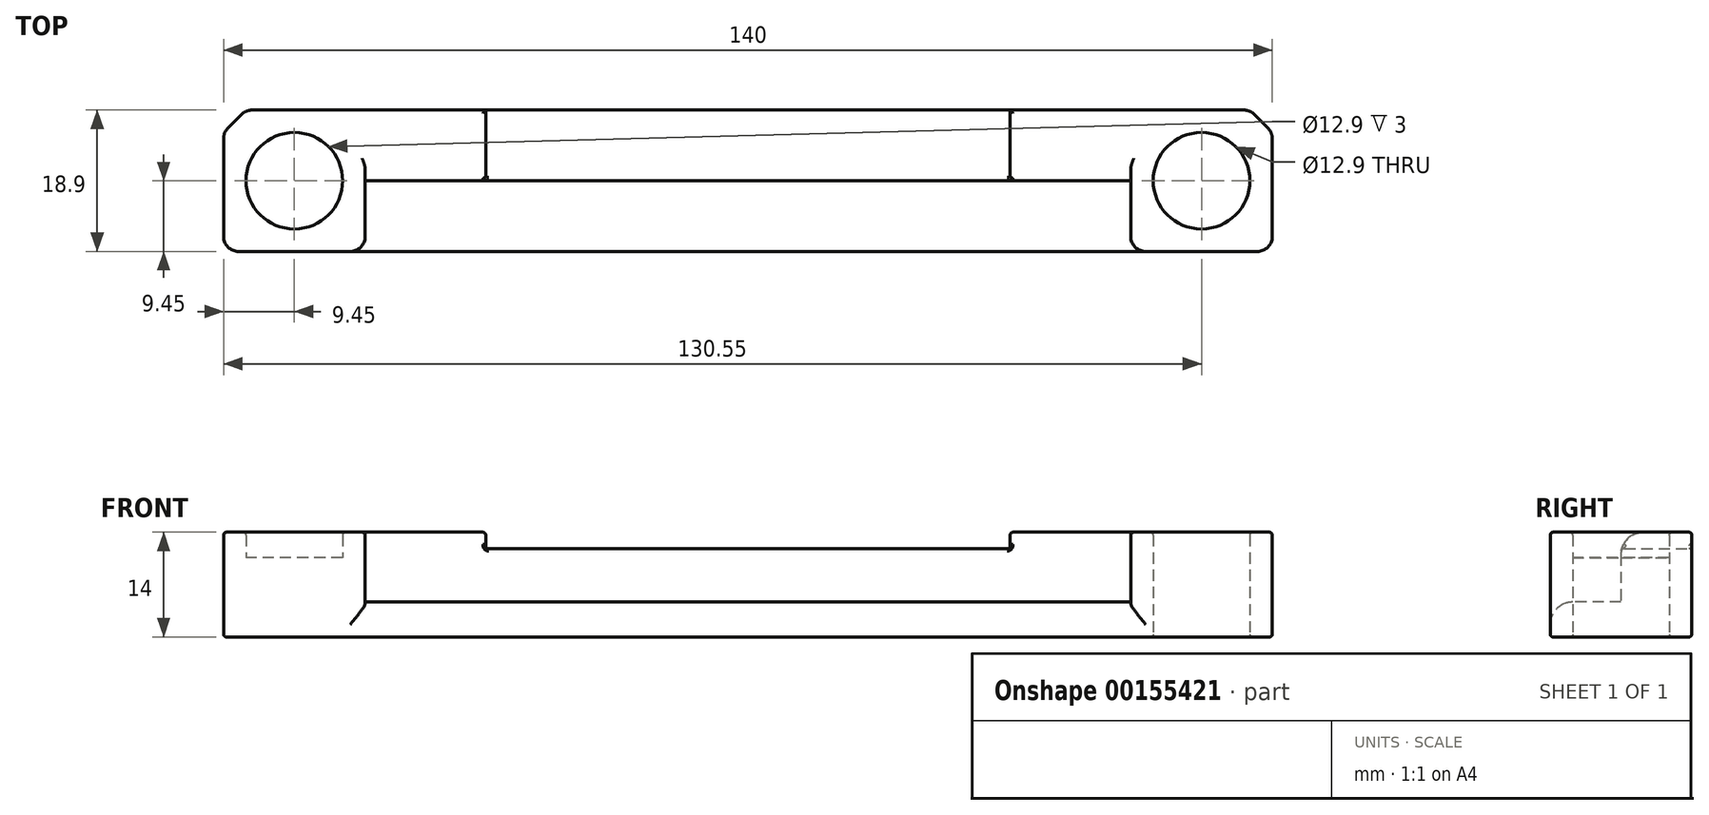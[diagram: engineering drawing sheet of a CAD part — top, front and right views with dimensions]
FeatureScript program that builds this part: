
annotation { "Feature Type Name" : "Feature", "Feature Type Description" : "" }
export const myFeature = defineFeature(function(context is Context, id is Id, definition is map)
    precondition{}
    {
        {
            assignVariable(context, id + "F0", {"name" : "PrintTolerance", "anyValue" : .2});
        }
        {
            assignVariable(context, id + "F1", {"name" : "MagnetThickness", "anyValue" : 3.4});
        }
        {
            assignVariable(context, id + "F2", {"name" : "OverallThickness", "anyValue" : 14});
        }
        {
            var Q0;
            Q0=qCreatedBy(makeId("Top.planeOp"),FACE);
            var sketch = newSketch(context, id + "F3", { "sketchPlane" : qUnion([Q0])});
            skCircle(sketch, "E0", {"center": v(9.45, 9.45) * mm, "radius": 6.45 * mm});
            skLineSegment(sketch, "E1", {"start": v(0, 0) * mm, "end": v(0, 15.9) * mm});
            skLineSegment(sketch, "E2", {"start": v(0, 15.9) * mm, "end": v(3, 18.9) * mm});
            skLineSegment(sketch, "E3", {"start": v(3, 18.9) * mm, "end": v(137, 18.9) * mm});
            skLineSegment(sketch, "E4", {"start": v(137, 18.9) * mm, "end": v(140, 15.9) * mm});
            skLineSegment(sketch, "E5", {"start": v(140, 15.9) * mm, "end": v(140, 0) * mm});
            skLineSegment(sketch, "E6", {"start": v(140, 0) * mm, "end": v(0, 0) * mm});
            skLineSegment(sketch, "E7", {"start": v(70, 18.9) * mm, "end": v(70, 0) * mm, "construction": true});
            skCircle(sketch, "E8.MirrorC", {"center": v(130.55, 9.45) * mm, "radius": 6.45 * mm});
            skLineSegment(sketch, "E9", {"start": v(0, 15.9) * mm, "end": v(140, 15.9) * mm, "construction": true});
            skLineSegment(sketch, "E10", {"start": v(18.9, 18.9) * mm, "end": v(18.9, 0) * mm});
            skLineSegment(sketch, "E11.MirrorCS", {"start": v(121.1, 18.9) * mm, "end": v(121.1, 0) * mm});
            skLineSegment(sketch, "E12", {"start": v(18.9, 9.45) * mm, "end": v(121.1, 9.45) * mm});
            skLineSegment(sketch, "E13", {"start": v(35, 9.45) * mm, "end": v(35, 18.9) * mm});
            skLineSegment(sketch, "E14.MirrorCS", {"start": v(105, 9.45) * mm, "end": v(105, 18.9) * mm});
            skSolve(sketch);
        }
        {
            var Q0;
            {var subQ3=sQuery(id+"F3.wireOp",EDGE,"E13");Q0=makeQuery(id+"F3.imprint","IMPRINT",FACE,{"disambiguationData":[TD([[makeQuery(id+"F3.imprint","IMPRINT",EDGE,{"derivedFrom":subQ3}),1.0]])]});}
            var Q1;
            {var subQ3=sQuery(id+"F3.wireOp",EDGE,"E14.MirrorCS");Q1=makeQuery(id+"F3.imprint","IMPRINT",FACE,{"disambiguationData":[TD([[makeQuery(id+"F3.imprint","IMPRINT",EDGE,{"derivedFrom":subQ3}),-1.0]])]});}
            var Q2;
            Q2=makeQuery(id+"F3.imprint","IMPRINT",FACE,{"disambiguationData":[TD([[makeQuery(id+"F3.imprint","IMPRINT",EDGE,{"derivedFrom":sQuery(id+"F3.wireOp",EDGE,"E0")}),-1.0]])]});
            var Q3;
            {var subQ4=sQuery(id+"F3.wireOp",EDGE,"E4");Q3=makeQuery(id+"F3.imprint","IMPRINT",FACE,{"disambiguationData":[TD([[makeQuery(id+"F3.imprint","IMPRINT",EDGE,{"derivedFrom":subQ4}),-1.0]])]});}
            extrude(context, id + "F4", {"entities" : qUnion([Q0, Q1, Q2, Q3]), "depth" : (getVariable(context, 'OverallThickness')) * mm});
        }
        {
            var Q0;
            {var subQ0=sQuery(id+"F3.wireOp",EDGE,"E13");Q0=makeQuery(id+"F3.imprint","IMPRINT",FACE,{"disambiguationData":[TD([[makeQuery(id+"F3.imprint","IMPRINT",EDGE,{"derivedFrom":subQ0}),-1.0]])]});}
            extrude(context, id + "F5", {"entities" : qUnion([Q0]), "operationType" : NewBodyOperationType.ADD, "depth" : (getVariable(context, 'OverallThickness') - 2 - getVariable(context, 'PrintTolerance')) * mm});
        }
        {
            var Q0;
            Q0=makeQuery(id+"F3.imprint","IMPRINT",FACE,{"disambiguationData":[TD([[makeQuery(id+"F3.imprint","IMPRINT",EDGE,{"derivedFrom":sQuery(id+"F3.wireOp",EDGE,"E0")}),1.0]])]});
            var Q1;
            Q1=makeQuery(id+"F3.imprint","IMPRINT",FACE,{"disambiguationData":[TD([[makeQuery(id+"F3.imprint","IMPRINT",EDGE,{"derivedFrom":sQuery(id+"F3.wireOp",EDGE,"E8.MirrorC")}),-1.0]])]});
            extrude(context, id + "F6", {"entities" : qUnion([Q0, Q1]), "operationType" : NewBodyOperationType.ADD, "depth" : (getVariable(context, 'OverallThickness') - getVariable(context, 'MagnetThickness')) * mm});
        }
        {
            var Q0;
            {var subQ5=sQuery(id+"F3.wireOp",EDGE,"E12");Q0=makeQuery(id+"F3.imprint","IMPRINT",FACE,{"disambiguationData":[TD([[makeQuery(id+"F3.imprint","IMPRINT",EDGE,{"derivedFrom":subQ5}),-1.0]])]});}
            extrude(context, id + "F7", {"entities" : qUnion([Q0]), "operationType" : NewBodyOperationType.ADD, "depth" : (getVariable(context, 'OverallThickness') / 3) * mm});
        }
        {
            var Q0;
            Q0=makeQuery(id+"F7.opExtrude","CAP_EDGE",EDGE,{"disambiguationData":[OSD([sQuery(id+"F3.wireOp",EDGE,"E6")])],"isStart":false});
            var Q1;
            Q1=makeQuery(id+"F7.opExtrude","CAP_EDGE",EDGE,{"disambiguationData":[OSD([sQuery(id+"F3.wireOp",EDGE,"E12")])],"isStart":false});
            var Q2;
            Q2=makeQuery(id+"F4.opExtrude","CAP_EDGE",EDGE,{"disambiguationData":[OSD([sQuery(id+"F3.wireOp",EDGE,"E12")])],"isStart":false});
            fillet(context, id + "F8", {"entities" : qUnion([Q0, Q1, Q2]), "radius" : 3 * mm, "tangentPropagation" : true, "allowEdgeOverflow" : false});
        }
        {
            var Q0;
            Q0=makeQuery(id+"F4.opExtrude","SWEPT_EDGE",EDGE,{"disambiguationData":[OSD([sQuery(id+"F3.wireOp",EDGE,"E1"),sQuery(id+"F3.wireOp",EDGE,"E6")])]});
            var Q1;
            Q1=makeQuery(id+"F4.opExtrude","SWEPT_EDGE",EDGE,{"disambiguationData":[OSD([sQuery(id+"F3.wireOp",EDGE,"E1"),sQuery(id+"F3.wireOp",EDGE,"E2")])]});
            var Q2;
            Q2=makeQuery(id+"F4.opExtrude","SWEPT_EDGE",EDGE,{"disambiguationData":[OSD([sQuery(id+"F3.wireOp",EDGE,"E2"),sQuery(id+"F3.wireOp",EDGE,"E3")])]});
            var Q3;
            Q3=makeQuery(id+"F4.opExtrude","SWEPT_EDGE",EDGE,{"disambiguationData":[OSD([sQuery(id+"F3.wireOp",EDGE,"E3"),sQuery(id+"F3.wireOp",EDGE,"E4")])]});
            var Q4;
            Q4=makeQuery(id+"F4.opExtrude","SWEPT_EDGE",EDGE,{"disambiguationData":[OSD([sQuery(id+"F3.wireOp",EDGE,"E4"),sQuery(id+"F3.wireOp",EDGE,"E5")])]});
            var Q5;
            Q5=makeQuery(id+"F4.opExtrude","SWEPT_EDGE",EDGE,{"disambiguationData":[OSD([sQuery(id+"F3.wireOp",EDGE,"E5"),sQuery(id+"F3.wireOp",EDGE,"E6")])]});
            var Q6;
            Q6=makeQuery(id+"F4.opExtrude","SWEPT_EDGE",EDGE,{"disambiguationData":[OSD([sQuery(id+"F3.wireOp",EDGE,"E6"),sQuery(id+"F3.wireOp",EDGE,"E10")])]});
            var Q7;
            Q7=makeQuery(id+"F4.opExtrude","SWEPT_EDGE",EDGE,{"disambiguationData":[OSD([sQuery(id+"F3.wireOp",EDGE,"E6"),sQuery(id+"F3.wireOp",EDGE,"E11.MirrorCS")])]});
            fillet(context, id + "F9", {"entities" : qUnion([Q0, Q1, Q2, Q3, Q4, Q5, Q6, Q7]), "radius" : 2 * mm, "tangentPropagation" : true, "allowEdgeOverflow" : false});
        }
        {
            var Q0;
            Q0=makeQuery(id+"F4.opExtrude","CAP_FACE",FACE,{"disambiguationData":[OSD([sQuery(id+"F3.wireOp",EDGE,"E0"),sQuery(id+"F3.wireOp",EDGE,"E1"),sQuery(id+"F3.wireOp",EDGE,"E2"),sQuery(id+"F3.wireOp",EDGE,"E3"),sQuery(id+"F3.wireOp",EDGE,"E4"),sQuery(id+"F3.wireOp",EDGE,"E5"),sQuery(id+"F3.wireOp",EDGE,"E6"),sQuery(id+"F3.wireOp",EDGE,"E8.MirrorC"),sQuery(id+"F3.wireOp",EDGE,"E10"),sQuery(id+"F3.wireOp",EDGE,"E11.MirrorCS"),sQuery(id+"F3.wireOp",EDGE,"E12")])],"isStart":false});
            var Q1;
            {var subQ0=sQuery(id+"F3.wireOp",EDGE,"E12");var subQ1=sQuery(id+"F3.wireOp",EDGE,"E11.MirrorCS");var subQ2=sQuery(id+"F3.wireOp",EDGE,"E10");var subQ3=sQuery(id+"F3.wireOp",EDGE,"E6");var subQ4=sQuery(id+"F3.wireOp",EDGE,"E8.MirrorC");var subQ5=sQuery(id+"F3.wireOp",EDGE,"E0");Q1=makeQuery(id+"F7.boolean.opBoolean","MERGE",FACE,{"derivedFrom":[makeQuery(id+"F6.boolean.opBoolean","MERGE",FACE,{"derivedFrom":[makeQuery(id+"F4.opExtrude","CAP_FACE",FACE,{"disambiguationData":[OSD([subQ5,sQuery(id+"F3.wireOp",EDGE,"E1"),sQuery(id+"F3.wireOp",EDGE,"E2"),sQuery(id+"F3.wireOp",EDGE,"E3"),sQuery(id+"F3.wireOp",EDGE,"E4"),sQuery(id+"F3.wireOp",EDGE,"E5"),subQ3,subQ4,subQ2,subQ1,subQ0])],"isStart":true}),makeQuery(id+"F6.opExtrude","CAP_FACE",FACE,{"disambiguationData":[OSD([subQ5])],"isStart":true}),makeQuery(id+"F6.opExtrude","CAP_FACE",FACE,{"disambiguationData":[OSD([subQ4])],"isStart":true})]}),makeQuery(id+"F7.opExtrude","CAP_FACE",FACE,{"disambiguationData":[OSD([subQ3,subQ2,subQ1,subQ0])],"isStart":true})]});}
            var Q2;
            Q2=makeQuery(id+"F5.opExtrude","CAP_FACE",FACE,{"disambiguationData":[OSD([sQuery(id+"F3.wireOp",EDGE,"E3"),sQuery(id+"F3.wireOp",EDGE,"E12"),sQuery(id+"F3.wireOp",EDGE,"E13"),sQuery(id+"F3.wireOp",EDGE,"E14.MirrorCS")])],"isStart":false});
            fillet(context, id + "F10", {"entities" : qUnion([Q0, Q1, Q2]), "radius" : (getVariable(context, 'PrintTolerance') * 2) * mm, "tangentPropagation" : true, "allowEdgeOverflow" : false});
        }
    });
